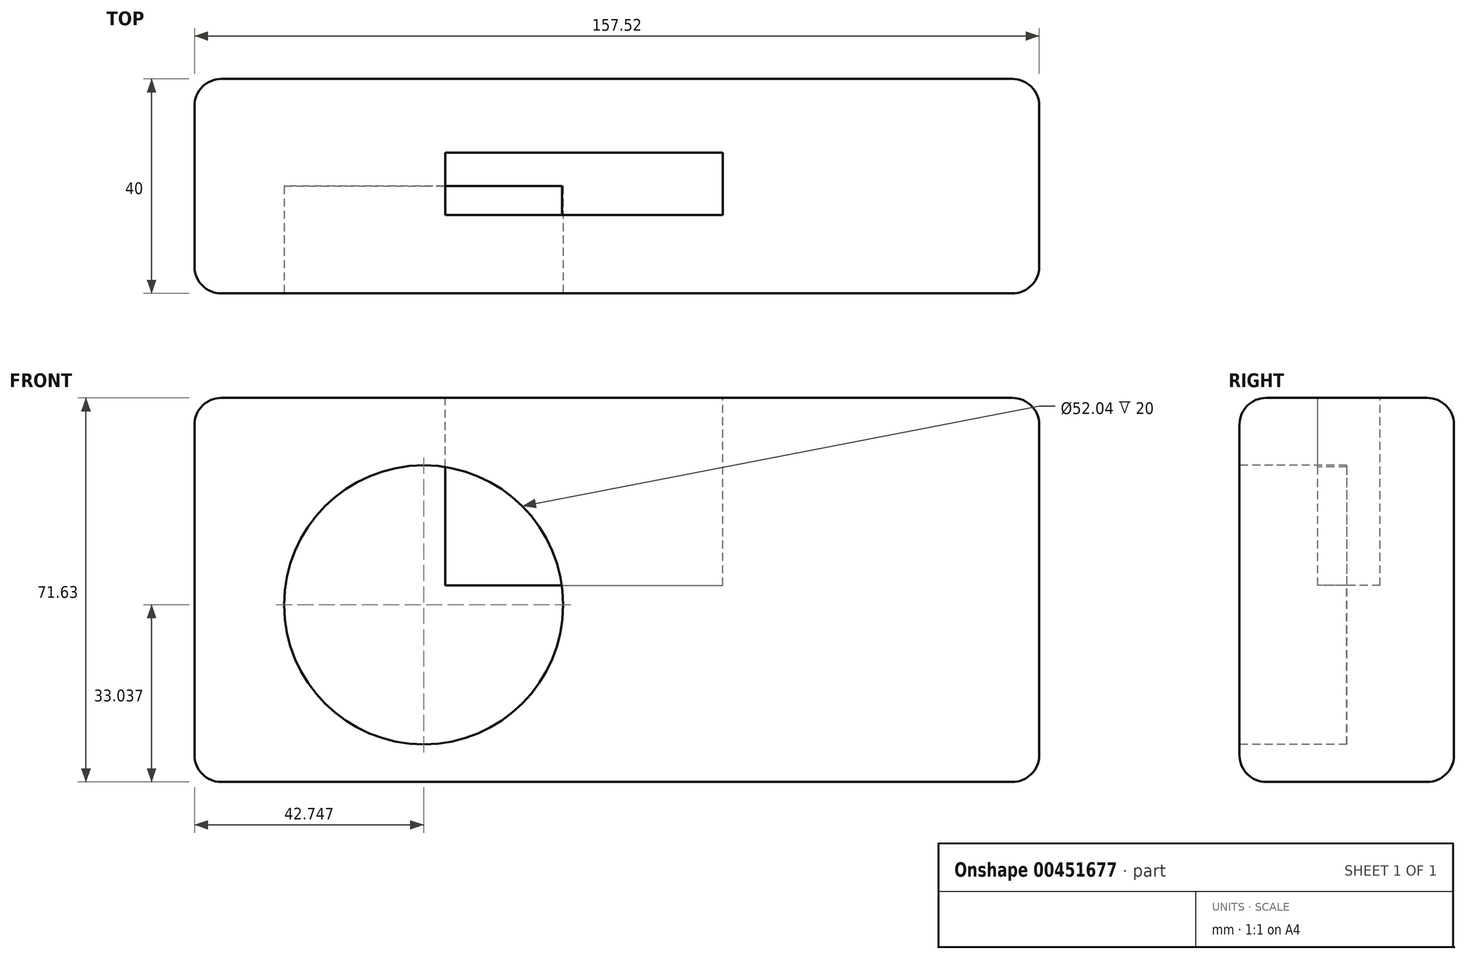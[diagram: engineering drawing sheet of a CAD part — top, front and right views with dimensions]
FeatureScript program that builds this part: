
annotation { "Feature Type Name" : "Feature", "Feature Type Description" : "" }
export const myFeature = defineFeature(function(context is Context, id is Id, definition is map)
    precondition{}
    {
        {
            var Q0;
            Q0=qCreatedBy(makeId("Front.planeOp"),FACE);
            var sketch = newSketch(context, id + "F0", { "sketchPlane" : qUnion([Q0])});
            skLineSegment(sketch, "E0.bottom", {"start": v(-78.76, 71.63) * mm, "end": v(78.76, 71.63) * mm});
            skLineSegment(sketch, "E0.top", {"start": v(-78.76, 0) * mm, "end": v(78.76, 0) * mm});
            skLineSegment(sketch, "E0.left", {"start": v(-78.76, 71.63) * mm, "end": v(-78.76, 0) * mm});
            skLineSegment(sketch, "E0.right", {"start": v(78.76, 71.63) * mm, "end": v(78.76, 0) * mm});
            skSolve(sketch);
        }
        {
            var Q0;
            Q0=makeQuery(id+"F0.imprint","IMPRINT",FACE,{"disambiguationData":[TD([[makeQuery(id+"F0.imprint","IMPRINT",EDGE,{"derivedFrom":sQuery(id+"F0.wireOp",EDGE,"E0.bottom")}),-1.0]])]});
            extrude(context, id + "F1", {"entities" : qUnion([Q0]), "depth" : 40 * mm});
        }
        {
            var Q0;
            Q0=makeQuery(id+"F1.opExtrude","CAP_EDGE",EDGE,{"disambiguationData":[OSD([sQuery(id+"F0.wireOp",EDGE,"E0.bottom")])],"isStart":false});
            var Q1;
            Q1=makeQuery(id+"F1.opExtrude","CAP_EDGE",EDGE,{"disambiguationData":[OSD([sQuery(id+"F0.wireOp",EDGE,"E0.bottom")])],"isStart":true});
            var Q2;
            Q2=makeQuery(id+"F1.opExtrude","CAP_EDGE",EDGE,{"disambiguationData":[OSD([sQuery(id+"F0.wireOp",EDGE,"E0.right")])],"isStart":false});
            var Q3;
            Q3=makeQuery(id+"F1.opExtrude","CAP_EDGE",EDGE,{"disambiguationData":[OSD([sQuery(id+"F0.wireOp",EDGE,"E0.right")])],"isStart":true});
            var Q4;
            Q4=makeQuery(id+"F1.opExtrude","SWEPT_EDGE",EDGE,{"disambiguationData":[OSD([sQuery(id+"F0.wireOp",EDGE,"E0.bottom"),sQuery(id+"F0.wireOp",EDGE,"E0.right")])]});
            var Q5;
            Q5=makeQuery(id+"F1.opExtrude","SWEPT_EDGE",EDGE,{"disambiguationData":[OSD([sQuery(id+"F0.wireOp",EDGE,"E0.bottom"),sQuery(id+"F0.wireOp",EDGE,"E0.left")])]});
            var Q6;
            Q6=makeQuery(id+"F1.opExtrude","CAP_EDGE",EDGE,{"disambiguationData":[OSD([sQuery(id+"F0.wireOp",EDGE,"E0.left")])],"isStart":true});
            var Q7;
            Q7=makeQuery(id+"F1.opExtrude","CAP_EDGE",EDGE,{"disambiguationData":[OSD([sQuery(id+"F0.wireOp",EDGE,"E0.left")])],"isStart":false});
            fillet(context, id + "F2", {"entities" : qUnion([Q0, Q1, Q2, Q3, Q4, Q5, Q6, Q7]), "radius" : 5 * mm, "tangentPropagation" : true, "allowEdgeOverflow" : false});
        }
        {
            var Q0;
            Q0=makeQuery(id+"F1.opExtrude","CAP_FACE",FACE,{"disambiguationData":[OSD([sQuery(id+"F0.wireOp",EDGE,"E0.bottom"),sQuery(id+"F0.wireOp",EDGE,"E0.top"),sQuery(id+"F0.wireOp",EDGE,"E0.left"),sQuery(id+"F0.wireOp",EDGE,"E0.right")])],"isStart":false});
            var sketch = newSketch(context, id + "F3", { "sketchPlane" : qUnion([Q0])});
            skCircle(sketch, "E1", {"center": v(-36.01, 33.04) * mm, "radius": 26.02 * mm});
            skSolve(sketch);
        }
        {
            var Q0;
            Q0=makeQuery(id+"F3.imprint","IMPRINT",FACE,{"disambiguationData":[TD([[makeQuery(id+"F3.imprint","IMPRINT",EDGE,{"derivedFrom":sQuery(id+"F3.wireOp",EDGE,"E1")}),1.0]])]});
            extrude(context, id + "F4", {"entities" : qUnion([Q0]), "operationType" : NewBodyOperationType.REMOVE, "oppositeDirection" : true, "depth" : 20 * mm});
        }
        {
            var Q0;
            Q0=makeQuery(id+"F1.opExtrude","SWEPT_FACE",FACE,{"disambiguationData":[OSD([sQuery(id+"F0.wireOp",EDGE,"E0.bottom")])]});
            var sketch = newSketch(context, id + "F5", { "sketchPlane" : qUnion([Q0])});
            skLineSegment(sketch, "E2.bottom", {"start": v(-32, -13.77) * mm, "end": v(19.78, -13.77) * mm});
            skLineSegment(sketch, "E2.top", {"start": v(-32, -25.4) * mm, "end": v(19.78, -25.4) * mm});
            skLineSegment(sketch, "E2.left", {"start": v(-32, -13.77) * mm, "end": v(-32, -25.4) * mm});
            skLineSegment(sketch, "E2.right", {"start": v(19.78, -13.77) * mm, "end": v(19.78, -25.4) * mm});
            skSolve(sketch);
        }
        {
            var Q0;
            Q0=makeQuery(id+"F5.imprint","IMPRINT",FACE,{"disambiguationData":[TD([[makeQuery(id+"F5.imprint","IMPRINT",EDGE,{"derivedFrom":sQuery(id+"F5.wireOp",EDGE,"E2.bottom")}),-1.0]])]});
            extrude(context, id + "F6", {"entities" : qUnion([Q0]), "operationType" : NewBodyOperationType.REMOVE, "oppositeDirection" : true, "depth" : 35 * mm});
        }
        {
            var Q0;
            Q0=makeQuery(id+"F1.opExtrude","CAP_EDGE",EDGE,{"disambiguationData":[OSD([sQuery(id+"F0.wireOp",EDGE,"E0.top")])],"isStart":false});
            fillet(context, id + "F7", {"entities" : qUnion([Q0]), "radius" : 5 * mm, "tangentPropagation" : true, "allowEdgeOverflow" : false});
        }
        {
            var Q0;
            Q0=sQuery(id+"F3.wireOp",EDGE,"E1");
            extrude(context, id + "F8", {"bodyType" : ToolBodyType.SURFACE, "surfaceEntities" : qUnion([Q0]), "depth" : 10 * mm});
        }
    });
